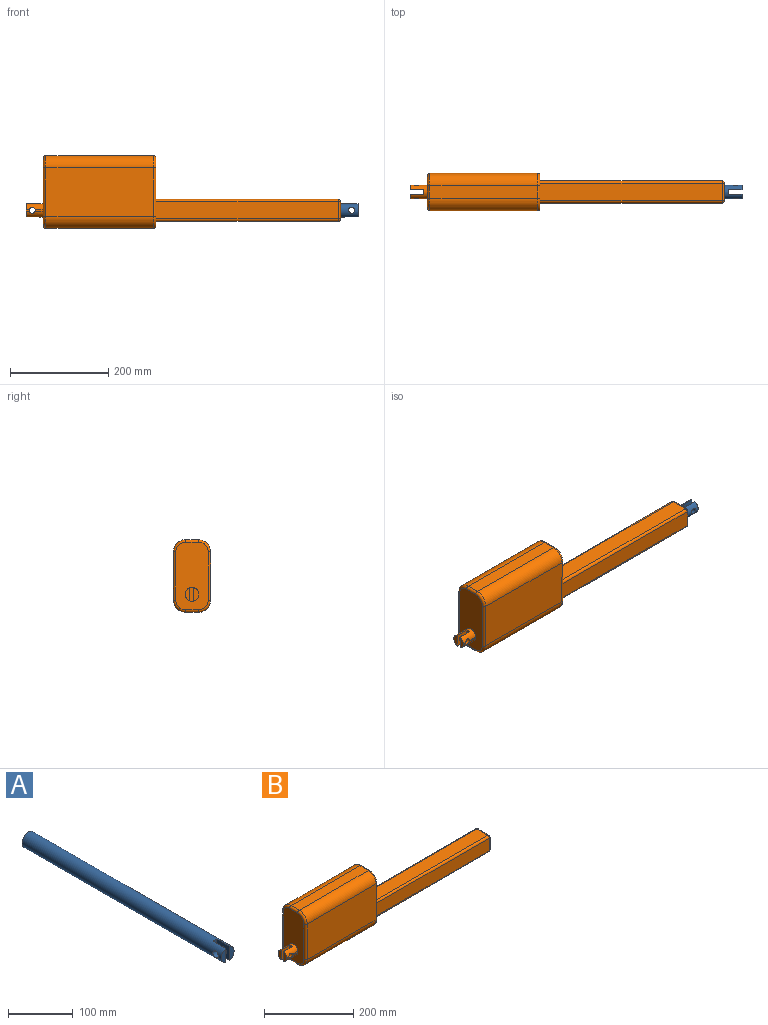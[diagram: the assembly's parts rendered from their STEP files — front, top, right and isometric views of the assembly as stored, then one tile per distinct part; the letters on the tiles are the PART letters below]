
ASSEMBLY  parts=2 mates=1
PART A: 12 faces, bbox 27.8x435.6x27.8 mm
  f0: plane 26.56x9.76mm, normal (0,-1,0), area 191.1mm2, adj f2,f6,f10
  f1: cylinder r=6.1mm len=12.2mm, axis (1,0,0), area 348.8mm2, adj f2,f3,f6,f10
  f2: cylinder r=13.9mm len=435.6mm, axis (0,1,0), area 37299.6mm2, adj f0,f1,f3,f4,f5,f6,f7,f8
  f3: plane 15.99x2.04mm, normal (1,0,0), area 32.5mm2, adj f1,f2,f7
  f4: plane 26.56x9.8mm, normal (0,-1,0), area 191.2mm2, adj f2,f9
  f5: plane 27.8x27.8mm, normal (0,1,0), area 607mm2, adj f2
  f6: plane 6.99x2.04mm, normal (1,0,0), area 14.1mm2, adj f0,f1,f2
  f7: plane 2.04x0.04mm, normal (0,-1,0), area 0.1mm2, adj f2,f3
  f8: cylinder r=6.1mm len=12.2mm, axis (1,0,0), area 349mm2, adj f2,f9
  f9: plane 27.5x26.56mm, normal (1,0,0), area 613.6mm2, adj f2,f4,f8,f11
  f10: plane 27.5x26.56mm, normal (-1,0,0), area 613.6mm2, adj f0,f1,f2,f11
  f11: plane 27.8x8.2mm, normal (0,-1,0), area 224.6mm2, adj f2,f9,f10
PART B: 56 faces, bbox 640.4x80.1x152.1 mm
  f0: plane 26.56x9.72mm, normal (-1,0,0), area 191mm2, adj f2,f11,f54
  f1: cylinder r=6.1mm len=12.2mm, axis (0,-1,0), area 348.6mm2, adj f2,f3,f11,f54
  f2: cylinder r=13.9mm len=35.6mm, axis (1,0,0), area 2342.7mm2, adj f0,f1,f3,f5,f10,f11,f12,f13
  f3: plane 16.09x3mm, normal (0,-1,0), area 47.9mm2, adj f1,f2,f12
  f4: plane 219x26mm, normal (0,0,1), area 5694mm2, adj f20,f22,f26,f34
  f5: plane 138x66mm, normal (-1,0,0), area 8157.6mm2, adj f2,f23,f24,f25,f26,f27,f28,f29
  f6: plane 219x26mm, normal (0,0,-1), area 5694mm2, adj f19,f21,f27,f35
  f7: plane 138x66mm, normal (1,0,0), area 6779.1mm2, adj f14,f15,f16,f17,f31,f32,f33,f34
  f8: plane 219x98mm, normal (0,-1,0), area 21462mm2, adj f21,f22,f30,f38
  f9: plane 219x98mm, normal (0,1,0), area 21462mm2, adj f19,f20,f23,f31
  f10: plane 26.56x9.8mm, normal (-1,0,0), area 191.2mm2, adj f2,f53
  f11: plane 7.09x3mm, normal (0,-1,0), area 20.9mm2, adj f0,f1,f2
  f12: plane 3x0.08mm, normal (-1,0,0), area 0.2mm2, adj f2,f3
  f13: cylinder r=6.1mm len=12.2mm, axis (0,-1,0), area 349mm2, adj f2,f53
  f14: plane 370.8x34.8mm, normal (0,-1,0), area 12903.8mm2, adj f7,f41,f47,f50
  f15: plane 370.8x34.8mm, normal (0,0,-1), area 12903.8mm2, adj f7,f44,f48,f50
  f16: plane 370.8x34.8mm, normal (0,1,0), area 12903.8mm2, adj f7,f39,f43,f44
  f17: plane 370.8x34.8mm, normal (0,0,1), area 12903.8mm2, adj f7,f39,f41,f42
  f18: plane 34.8x34.8mm, normal (1,0,0), area 604.1mm2, adj f42,f43,f47,f48,f51
  f19: cylinder r=25mm len=219mm, axis (1,0,0), area 8600.1mm2, adj f6,f9,f25,f33
  f20: cylinder r=25mm len=219mm, axis (-1,0,0), area 8600.1mm2, adj f4,f9,f24,f32
  f21: cylinder r=25mm len=219mm, axis (-1,0,0), area 8600.1mm2, adj f6,f8,f29,f37
  f22: cylinder r=25mm len=219mm, axis (1,0,0), area 8600.1mm2, adj f4,f8,f28,f36
  f23: cylinder r=5mm len=98mm, axis (0,0,-1), area 769.7mm2, adj f5,f9,f24,f25
  f24: torus R=20mm, axis (1,0,0), area 286mm2, adj f5,f20,f23,f26
  f25: torus R=20mm, axis (1,0,0), area 286mm2, adj f5,f19,f23,f27
  f26: cylinder r=5mm len=26mm, axis (0,-1,0), area 204.2mm2, adj f4,f5,f24,f28
  f27: cylinder r=5mm len=26mm, axis (0,1,0), area 204.2mm2, adj f5,f6,f25,f29
  f28: torus R=20mm, axis (1,0,0), area 286mm2, adj f5,f22,f26,f30
  f29: torus R=20mm, axis (1,0,0), area 286mm2, adj f5,f21,f27,f30
  f30: cylinder r=5mm len=98mm, axis (0,0,1), area 769.7mm2, adj f5,f8,f28,f29
  f31: cylinder r=5mm len=98mm, axis (0,0,1), area 769.7mm2, adj f7,f9,f32,f33
  f32: torus R=20mm, axis (1,0,0), area 286mm2, adj f7,f20,f31,f34
  f33: torus R=20mm, axis (1,0,0), area 286mm2, adj f7,f19,f31,f35
  f34: cylinder r=5mm len=26mm, axis (0,1,0), area 204.2mm2, adj f4,f7,f32,f36
  f35: cylinder r=5mm len=26mm, axis (0,-1,0), area 204.2mm2, adj f6,f7,f33,f37
  f36: torus R=20mm, axis (1,0,0), area 286mm2, adj f7,f22,f34,f38
  f37: torus R=20mm, axis (1,0,0), area 286mm2, adj f7,f21,f35,f38
  f38: cylinder r=5mm len=98mm, axis (0,0,-1), area 769.7mm2, adj f7,f8,f36,f37
  f39: cylinder r=5mm len=370.8mm, axis (-1,0,0), area 2912.3mm2, adj f7,f16,f17,f40
  f40: sphere r=5mm, area 39.3mm2, adj f39,f42,f43
  f41: cylinder r=5mm len=370.8mm, axis (1,0,0), area 2912.3mm2, adj f7,f14,f17,f45
  f42: cylinder r=5mm len=34.8mm, axis (0,1,0), area 273.3mm2, adj f17,f18,f40,f45
  f43: cylinder r=5mm len=34.8mm, axis (0,0,-1), area 273.3mm2, adj f16,f18,f40,f46
  f44: cylinder r=5mm len=370.8mm, axis (1,0,0), area 2912.3mm2, adj f7,f15,f16,f46
  f45: sphere r=5mm, area 39.3mm2, adj f41,f42,f47
  f46: sphere r=5mm, area 39.3mm2, adj f43,f44,f48
  f47: cylinder r=5mm len=34.8mm, axis (0,0,1), area 273.3mm2, adj f14,f18,f45,f49
  f48: cylinder r=5mm len=34.8mm, axis (0,-1,0), area 273.3mm2, adj f15,f18,f46,f49
  f49: sphere r=5mm, area 39.3mm2, adj f47,f48,f50
  f50: cylinder r=5mm len=370.8mm, axis (-1,0,0), area 2912.3mm2, adj f7,f14,f15,f49
  f51: cylinder r=13.9mm len=400mm, axis (1,0,0), area 34934.5mm2, adj f18,f52
  f52: plane 27.8x27.8mm, normal (1,0,0), area 607mm2, adj f51
  f53: plane 27.5x26.56mm, normal (0,-1,0), area 613.6mm2, adj f2,f10,f13,f55
  f54: plane 27.5x26.56mm, normal (0,1,0), area 613.6mm2, adj f0,f1,f2,f55
  f55: plane 27.8x8.2mm, normal (-1,0,0), area 224.6mm2, adj f2,f53,f54
PLACE A rot(axis=(0,0,1),90deg) t=(-92.73,-233.55,-165.08)mm
PLACE B rot(axis=(1,0,0),0.1deg) t=(-400.83,-233.61,-127.68)mm fixed
MATE slider A.f2 <-> B.f51  axis (1,0,0) through (-310.53,-233.55,-165.08)mm
